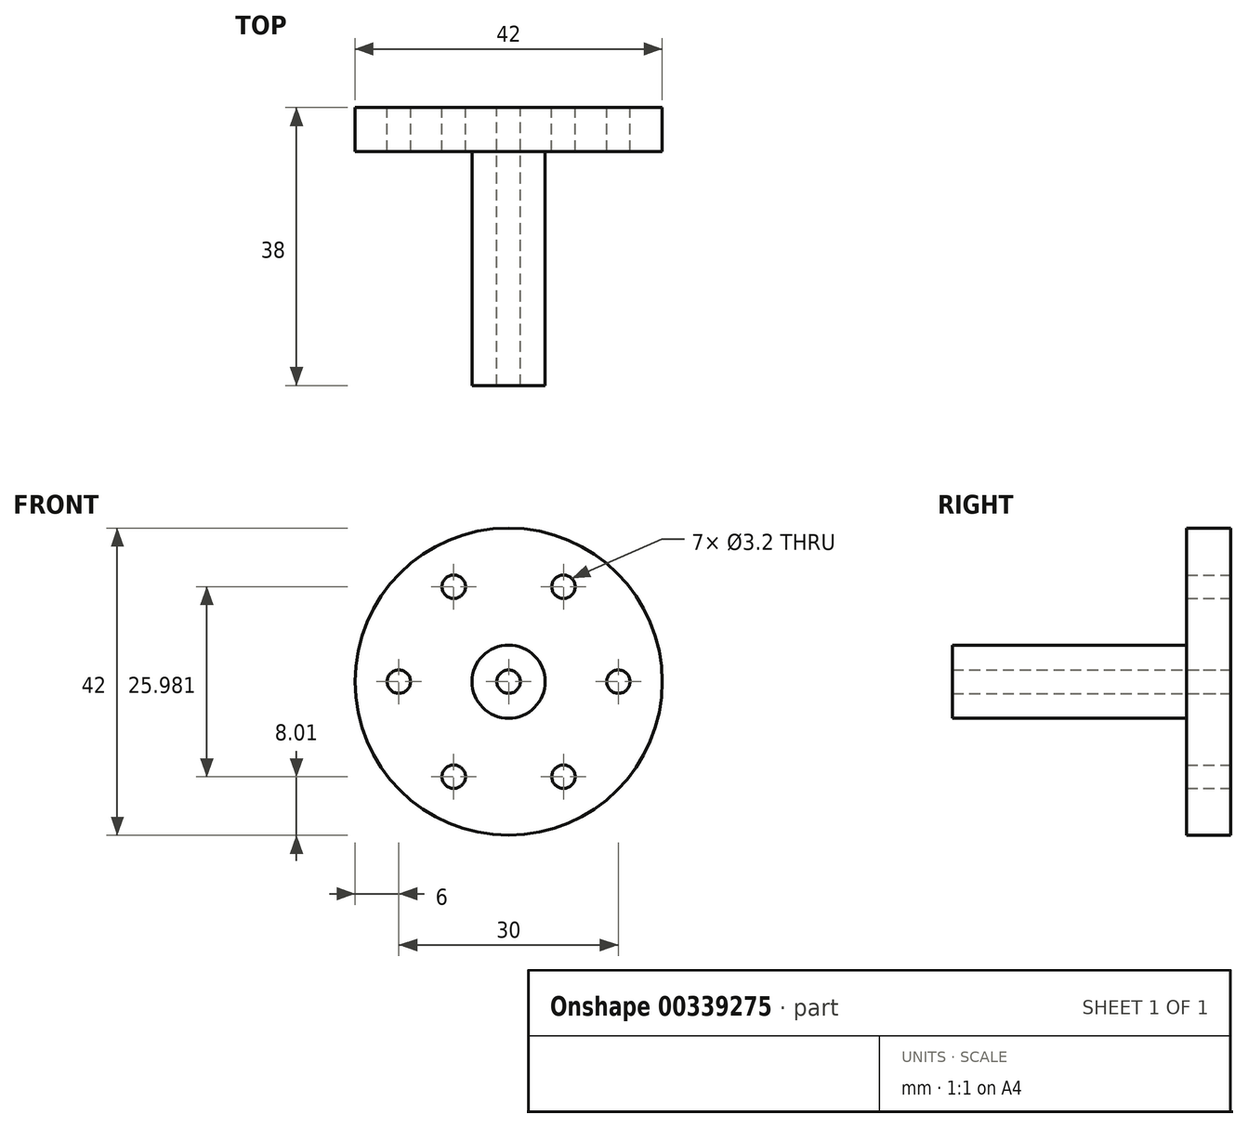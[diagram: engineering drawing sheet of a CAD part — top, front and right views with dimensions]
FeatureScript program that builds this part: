
annotation { "Feature Type Name" : "Feature", "Feature Type Description" : "" }
export const myFeature = defineFeature(function(context is Context, id is Id, definition is map)
    precondition{}
    {
        {
            var Q0;
            Q0=qCreatedBy(makeId("Front.planeOp"),FACE);
            var sketch = newSketch(context, id + "F0", { "sketchPlane" : qUnion([Q0])});
            skCircle(sketch, "E0", {"center": v(0, 0) * mm, "radius": 21 * mm});
            skCircle(sketch, "E1", {"center": v(0, 0) * mm, "radius": 5 * mm});
            skCircle(sketch, "E2", {"center": v(0, 0) * mm, "radius": 15 * mm, "construction": true});
            skCircle(sketch, "E3", {"center": v(15, 0) * mm, "radius": 2 * mm});
            skCircle(sketch, "E4.1.0", {"center": v(7.5, -13) * mm, "radius": 2 * mm});
            skCircle(sketch, "E4.2.0", {"center": v(-7.5, -13) * mm, "radius": 2 * mm});
            skCircle(sketch, "E4.3.0", {"center": v(-15, 0) * mm, "radius": 2 * mm});
            skCircle(sketch, "E4.4.0", {"center": v(-7.5, 13) * mm, "radius": 2 * mm});
            skCircle(sketch, "E4.5.0", {"center": v(7.5, 13) * mm, "radius": 2 * mm});
            skLineSegment(sketch, "E4.anchor1", {"start": v(0, 0) * mm, "end": v(15, 0) * mm, "construction": true});
            skLineSegment(sketch, "E4.anchor2", {"start": v(0, 0) * mm, "end": v(7.5, 13) * mm, "construction": true});
            skCircle(sketch, "E5", {"center": v(0, 0) * mm, "radius": 2 * mm});
            skSolve(sketch);
        }
        {
            var Q0;
            Q0=makeQuery(id+"F0.imprint","IMPRINT",FACE,{"disambiguationData":[TD([[makeQuery(id+"F0.imprint","IMPRINT",EDGE,{"derivedFrom":sQuery(id+"F0.wireOp",EDGE,"E0")}),1.0]])]});
            var Q1;
            Q1=makeQuery(id+"F0.imprint","IMPRINT",FACE,{"disambiguationData":[TD([[makeQuery(id+"F0.imprint","IMPRINT",EDGE,{"derivedFrom":sQuery(id+"F0.wireOp",EDGE,"E4.3.0")}),1.0]])]});
            var Q2;
            Q2=makeQuery(id+"F0.imprint","IMPRINT",FACE,{"disambiguationData":[TD([[makeQuery(id+"F0.imprint","IMPRINT",EDGE,{"derivedFrom":sQuery(id+"F0.wireOp",EDGE,"E4.4.0")}),1.0]])]});
            var Q3;
            Q3=makeQuery(id+"F0.imprint","IMPRINT",FACE,{"disambiguationData":[TD([[makeQuery(id+"F0.imprint","IMPRINT",EDGE,{"derivedFrom":sQuery(id+"F0.wireOp",EDGE,"E4.5.0")}),1.0]])]});
            var Q4;
            Q4=makeQuery(id+"F0.imprint","IMPRINT",FACE,{"disambiguationData":[TD([[makeQuery(id+"F0.imprint","IMPRINT",EDGE,{"derivedFrom":sQuery(id+"F0.wireOp",EDGE,"E3")}),1.0]])]});
            var Q5;
            Q5=makeQuery(id+"F0.imprint","IMPRINT",FACE,{"disambiguationData":[TD([[makeQuery(id+"F0.imprint","IMPRINT",EDGE,{"derivedFrom":sQuery(id+"F0.wireOp",EDGE,"E4.1.0")}),1.0]])]});
            var Q6;
            Q6=makeQuery(id+"F0.imprint","IMPRINT",FACE,{"disambiguationData":[TD([[makeQuery(id+"F0.imprint","IMPRINT",EDGE,{"derivedFrom":sQuery(id+"F0.wireOp",EDGE,"E4.2.0")}),1.0]])]});
            extrude(context, id + "F1", {"entities" : qUnion([Q0, Q1, Q2, Q3, Q4, Q5, Q6]), "depth" : 6 * mm});
        }
        {
            var Q0;
            Q0=makeQuery(id+"F0.imprint","IMPRINT",FACE,{"disambiguationData":[TD([[makeQuery(id+"F0.imprint","IMPRINT",EDGE,{"derivedFrom":sQuery(id+"F0.wireOp",EDGE,"E1")}),1.0]])]});
            var Q1;
            Q1=makeQuery(id+"F0.imprint","IMPRINT",FACE,{"disambiguationData":[TD([[makeQuery(id+"F0.imprint","IMPRINT",EDGE,{"derivedFrom":sQuery(id+"F0.wireOp",EDGE,"E5")}),1.0]])]});
            extrude(context, id + "F2", {"entities" : qUnion([Q0, Q1]), "operationType" : NewBodyOperationType.ADD, "depth" : 38 * mm});
        }
        {
            var Q0;
            Q0=sQuery(id+"F0.wireOp",VERTEX,"E4.3.0.center");
            var Q1;
            Q1=sQuery(id+"F0.wireOp",VERTEX,"E4.4.0.center");
            var Q2;
            Q2=sQuery(id+"F0.wireOp",VERTEX,"E4.5.0.center");
            var Q3;
            Q3=sQuery(id+"F0.wireOp",VERTEX,"E3.center");
            var Q4;
            Q4=sQuery(id+"F0.wireOp",VERTEX,"E4.1.0.center");
            var Q5;
            Q5=sQuery(id+"F0.wireOp",VERTEX,"E4.2.0.center");
            var Q6;
            Q6=sQuery(id+"F0.wireOp",VERTEX,"E0.center");
            var Q7;
            Q7=makeQuery(id+"F1.opExtrude","SWEPT_BODY",BODY,{"disambiguationData":[OSD([sQuery(id+"F0.wireOp",EDGE,"E0"),sQuery(id+"F0.wireOp",EDGE,"E1")])]});
            hole(context, id + "F3", {"style" : HoleStyle.SIMPLE, "endStyle" : HoleEndStyle.THROUGH, "oppositeDirection" : true, "standardTappedOrClearance" : lookupTablePath({ "standard" : "ISO", "engagement" : "75%", "pitch" : "0.75 mm", "size" : "M4", "type" : "Tapped" }), "standardBlindInLast" : lookupTablePath({ "standard" : "ISO", "engagement" : "75%", "pitch" : "0.75 mm", "size" : "M4", "type" : "Tapped" }), "holeDiameter" : 3.2 * mm, "showTappedDepth" : true, "isTappedThrough" : true, "tappedDepth" : 12 * mm, "tapClearance" : 3, "locations" : qUnion([Q0, Q1, Q2, Q3, Q4, Q5, Q6]), "scope" : qUnion([Q7])});
        }
    });
